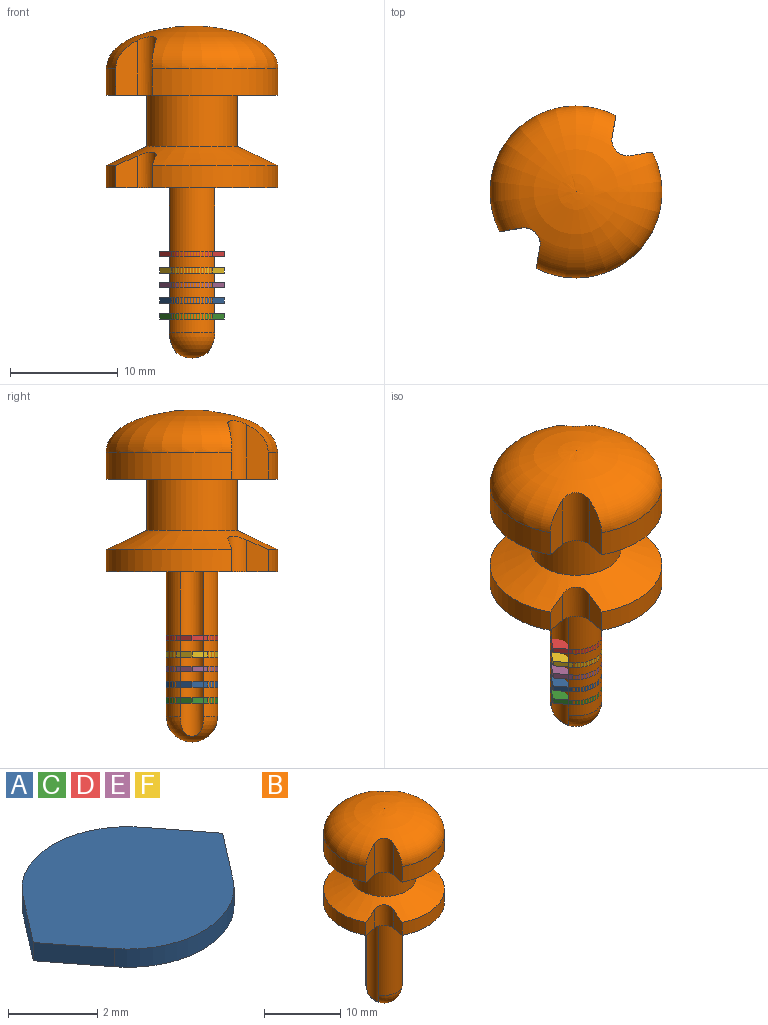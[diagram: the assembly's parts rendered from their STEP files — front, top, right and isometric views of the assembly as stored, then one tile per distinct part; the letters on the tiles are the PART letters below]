
ASSEMBLY  parts=6 mates=5
PART A: 8 faces, bbox 6x4.8x0.5 mm
  f0: plane 1.45x1.12mm, normal (0.79,0.61,0), area 0.9mm2, adj f1,f5,f6,f7
  f1: cylinder r=2.38mm len=3.76mm, axis (0,0,-1), area 2.2mm2, adj f0,f2,f6,f7
  f2: plane 1.45x1.12mm, normal (-0.79,0.61,0), area 0.9mm2, adj f1,f3,f6,f7
  f3: plane 1.45x1.12mm, normal (-0.79,-0.61,0), area 0.9mm2, adj f2,f4,f6,f7
  f4: cylinder r=2.38mm len=3.76mm, axis (0,0,-1), area 2.2mm2, adj f3,f5,f6,f7
  f5: plane 1.45x1.12mm, normal (0.79,-0.61,0), area 0.9mm2, adj f0,f4,f6,f7
  f6: plane 6x4.75mm, normal (0,0,1), area 19mm2, adj f0,f1,f2,f3,f4,f5
  f7: plane 6x4.75mm, normal (0,0,-1), area 19mm2, adj f0,f1,f2,f3,f4,f5
PART B: 26 faces, bbox 47.8x47.8x61.6 mm
  f0: plane 15.92x15.92mm, normal (0,0,-1), area 127.8mm2, adj f1,f17,f19,f20,f21,f22,f23,f24
  f1: cylinder r=4.18mm len=8.36mm, axis (0,0,-1), area 124.4mm2, adj f0,f2
  f2: cone r=7.96mm half-angle=65deg, axis (0,0,-1), area 141.3mm2, adj f1,f3,f10,f11,f12,f13,f14,f15
  f3: cylinder r=7.96mm len=11.65mm, axis (0,0,-1), area 42mm2, adj f2,f4,f10,f16
  f4: plane 15.92x15.92mm, normal (0,0,-1), area 167.6mm2, adj f3,f5,f7,f8,f9,f10,f11,f12
  f5: cylinder r=1.25mm len=15.22mm, axis (0,0,1), area 38.5mm2, adj f4,f6,f7,f9
  f6: sphere r=2.38mm, area 28mm2, adj f5,f7,f8,f9
  f7: cylinder r=2.38mm len=13.38mm, axis (0,0,-1), area 69.9mm2, adj f4,f5,f6,f8
  f8: cylinder r=1.25mm len=15.22mm, axis (0,0,1), area 38.5mm2, adj f4,f6,f7,f9
  f9: cylinder r=2.38mm len=13.38mm, axis (0,0,-1), area 69.9mm2, adj f4,f5,f6,f8
  f10: plane 3.05x2.07mm, normal (0.98,-0.17,0), area 5.1mm2, adj f2,f3,f4,f11
  f11: cylinder r=1.5mm len=3.31mm, axis (0,0,1), area 9.2mm2, adj f2,f4,f10,f12
  f12: plane 3.05x2.07mm, normal (-0.17,0.98,0), area 5.1mm2, adj f2,f4,f11,f13
  f13: cylinder r=7.96mm len=11.65mm, axis (0,0,-1), area 42mm2, adj f2,f4,f12,f14
  f14: plane 3.05x2.07mm, normal (-0.98,0.17,0), area 5.1mm2, adj f2,f4,f13,f15
  f15: cylinder r=1.5mm len=3.31mm, axis (0,0,1), area 9.2mm2, adj f2,f4,f14,f16
  f16: plane 3.05x2.07mm, normal (0.17,-0.98,0), area 5.1mm2, adj f2,f3,f4,f15
  f17: cylinder r=1.5mm len=5.44mm, axis (0,0,1), area 15.3mm2, adj f0,f18,f19,f25
  f18: revolved ~15.01x15.01mm, area 29mm2, adj f17,f19,f20,f21,f22,f23,f24,f25
  f19: plane 5.08x1.98mm, normal (-0.98,0.17,0), area 8.6mm2, adj f0,f17,f18,f20
  f20: cylinder r=7.96mm len=11.65mm, axis (0,0,-1), area 50.4mm2, adj f0,f18,f19,f21
  f21: plane 5.08x1.98mm, normal (-0.17,0.98,0), area 8.6mm2, adj f0,f18,f20,f22
  f22: cylinder r=1.5mm len=5.44mm, axis (0,0,1), area 15.3mm2, adj f0,f18,f21,f23
  f23: plane 5.08x1.98mm, normal (0.98,-0.17,0), area 8.6mm2, adj f0,f18,f22,f24
  f24: cylinder r=7.96mm len=11.65mm, axis (0,0,-1), area 50.4mm2, adj f0,f18,f23,f25
  f25: plane 36.92x33.82mm, normal (0.17,-0.98,0), area 8.6mm2, adj f0,f17,f18,f24
PART C: same geometry as A
PART D: same geometry as A
PART E: same geometry as A
PART F: same geometry as A
PLACE A t=(2.18,-7.49,-5.26)mm
PLACE B t=(2.18,-7.49,-10.33)mm
PLACE C t=(2.18,-7.49,-6.72)mm
PLACE D t=(2.18,-7.49,-0.96)mm
PLACE E t=(2.18,-7.49,-3.85)mm
PLACE F t=(2.18,-7.49,-2.47)mm
MATE cylindrical E.f1 <-> B.f1  axis (0,0,-1) through (2.18,-7.49,-3.6)mm
MATE cylindrical F.f4 <-> B.f1  axis (0,0,-1) through (2.18,-7.49,-2.22)mm
MATE cylindrical A.f1 <-> B.f1  axis (0,0,-1) through (2.18,-7.49,-5.01)mm
MATE cylindrical D.f1 <-> B.f1  axis (0,0,-1) through (2.18,-7.49,-0.71)mm
MATE cylindrical C.f1 <-> B.f1  axis (0,0,-1) through (2.18,-7.49,-6.22)mm
